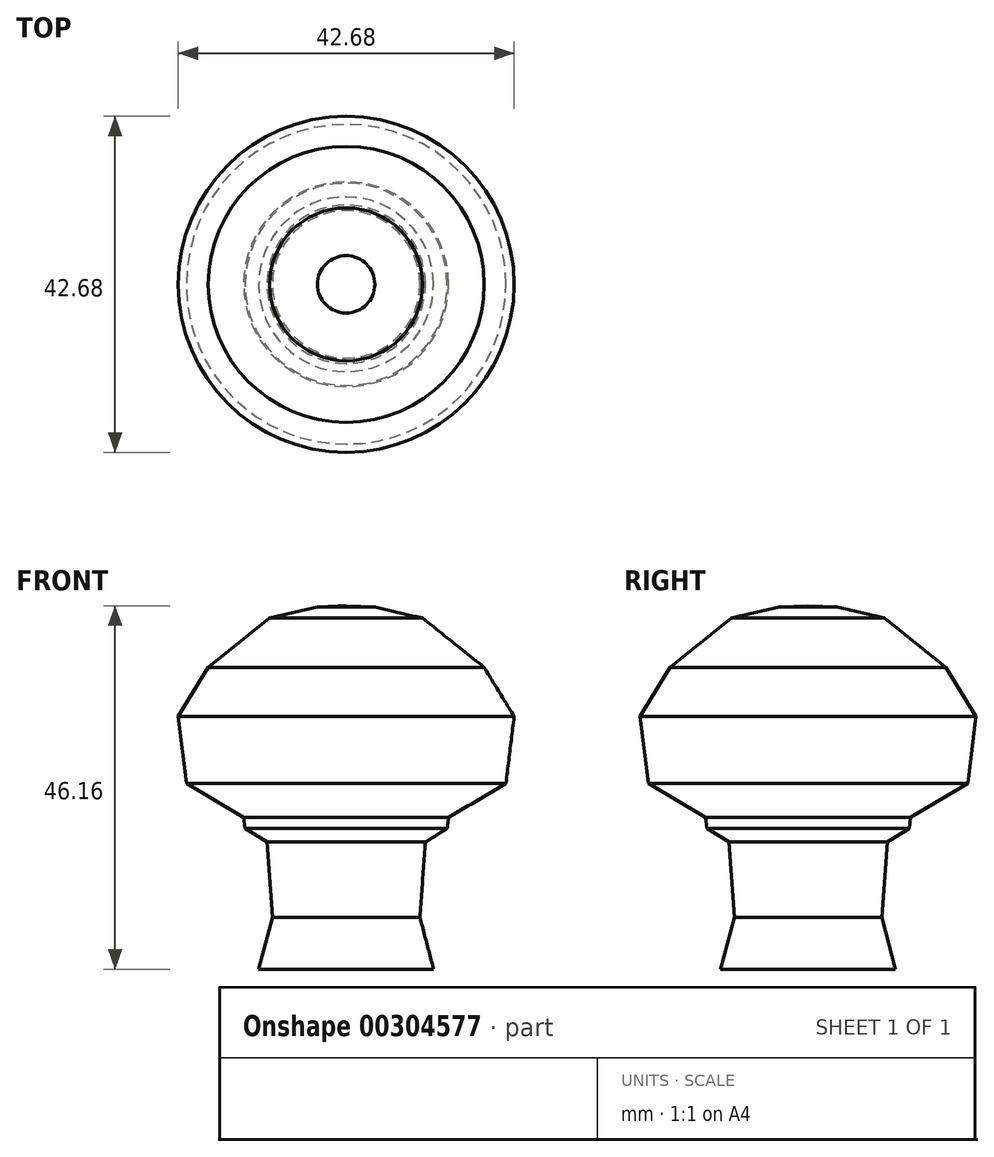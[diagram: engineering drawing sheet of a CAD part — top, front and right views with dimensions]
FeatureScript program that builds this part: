
annotation { "Feature Type Name" : "Feature", "Feature Type Description" : "" }
export const myFeature = defineFeature(function(context is Context, id is Id, definition is map)
    precondition{}
    {
        {
            var Q0;
            Q0=qCreatedBy(makeId("Front.planeOp"),FACE);
            var sketch = newSketch(context, id + "F0", { "sketchPlane" : qUnion([Q0])});
            skLineSegment(sketch, "E0", {"start": v(-2.17, -115.39) * mm, "end": v(6.5, -82.42) * mm});
            skLineSegment(sketch, "E1", {"start": v(6.5, -82.42) * mm, "end": v(3.04, -34.7) * mm});
            skLineSegment(sketch, "E2", {"start": v(3.04, -34.7) * mm, "end": v(-10.84, -26.03) * mm});
            skLineSegment(sketch, "E3", {"start": v(-10.84, -26.03) * mm, "end": v(-11.71, -19.09) * mm});
            skLineSegment(sketch, "E4", {"start": v(-11.71, -19.09) * mm, "end": v(-48.15, 2.6) * mm});
            skLineSegment(sketch, "E5", {"start": v(-48.15, 2.6) * mm, "end": v(-53.36, 45.11) * mm});
            skLineSegment(sketch, "E6", {"start": v(-53.36, 45.11) * mm, "end": v(-34.27, 76.35) * mm});
            skLineSegment(sketch, "E7", {"start": v(-34.27, 76.35) * mm, "end": v(4.77, 107.58) * mm});
            skLineSegment(sketch, "E8", {"start": v(4.77, 107.58) * mm, "end": v(35.14, 114.52) * mm});
            skLineSegment(sketch, "E9", {"start": v(35.14, 114.52) * mm, "end": v(53.36, 115.39) * mm});
            skLineSegment(sketch, "E10", {"start": v(53.36, 115.39) * mm, "end": v(53.36, -115.39) * mm});
            skLineSegment(sketch, "E11", {"start": v(53.36, -115.39) * mm, "end": v(-2.17, -115.39) * mm});
            skSolve(sketch);
        }
        {
            var Q0;
            Q0=makeQuery(id+"F0.imprint","IMPRINT",FACE,{"disambiguationData":[TD([[makeQuery(id+"F0.imprint","IMPRINT",EDGE,{"derivedFrom":sQuery(id+"F0.wireOp",EDGE,"E0")}),-1.0]])]});
            var Q1;
            Q1=sQuery(id+"F0.wireOp",EDGE,"E10");
            revolve(context, id + "F1", {"entities" : qUnion([Q0]), "axis" : qUnion([Q1]), "revolveType" : RevolveType.FULL});
        }
        {
            var Q0;
            Q0=makeQuery(id+"F1.opRevolve","SWEPT_BODY",BODY,{"disambiguationData":[OSD([sQuery(id+"F0.wireOp",EDGE,"E0"),sQuery(id+"F0.wireOp",EDGE,"E1"),sQuery(id+"F0.wireOp",EDGE,"E2"),sQuery(id+"F0.wireOp",EDGE,"E3"),sQuery(id+"F0.wireOp",EDGE,"E4"),sQuery(id+"F0.wireOp",EDGE,"E5"),sQuery(id+"F0.wireOp",EDGE,"E6"),sQuery(id+"F0.wireOp",EDGE,"E7"),sQuery(id+"F0.wireOp",EDGE,"E8"),sQuery(id+"F0.wireOp",EDGE,"E9"),sQuery(id+"F0.wireOp",EDGE,"E10"),sQuery(id+"F0.wireOp",EDGE,"E11")])]});
            var Q1;
            Q1=qCreatedBy(makeId("Origin.pointOp"),VERTEX);
            transform(context, id + "F2", {"entities" : qUnion([Q0]), "transformType" : TransformType.SCALE_UNIFORMLY, "scale" : .2, "scalePoint" : qUnion([Q1]), "makeCopy" : false});
        }
    });
